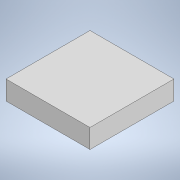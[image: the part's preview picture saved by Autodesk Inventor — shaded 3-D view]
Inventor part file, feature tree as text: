
AUTODESK INVENTOR PART (.ipt)
format: ipt  version: 2021 (Build 250183000, 183)  size: 5,559,296 bytes
history: native  units: mm
features: other x26, surface_op x18, fillet x14, sketch x9, extrude x6, revolve x4, plane x3, pattern_circular x2, loft x1
ambient origin geometry x8: Origin, YZ Plane, XZ Plane, XY Plane, X Axis, Y Axis, Z Axis, Center Point
bodies: Solid1 (feature_tree)
feature tree (83):
  plane  "Work Plane1"
  plane  "Work Plane2"
  plane  "Work Plane3"
  surface_op  "Trim1"
  surface_op  "Trim2"
  surface_op  "Trim3"
  surface_op  "Trim4"
  fillet  "Fillet5"  Radius=138.0mm
  fillet  "Fillet6"  Radius=95.0mm
  fillet  "Fillet7"  Radius=33.0mm
  fillet  "Fillet8"  Radius=110.0mm
  fillet  "Fillet9"  Radius=200.0mm
  fillet  "Fillet10"  Radius=463.0mm
  pattern_circular  "Circular Pattern1"  Count=3  [1 undecoded]
  surface_op  "Stitch Surface1"
  pattern_circular  "Circular Pattern2"  Count=20  [1 undecoded]
  surface_op  "Trim5"
  surface_op  "Trim6"
  surface_op  "Trim7"
  surface_op  "Trim8"
  surface_op  "Trim9"
  extrude  "Extrusion1"  Depth=16.0mm
  surface_op  "Sculpt1"
  sketch  "Sketch1"  dims[d6=84.0mm]
  other  "Srf1"
  sketch  "Sketch2"  dims[d7=12.566371mm d8=30.0mm]
  other  "Srf2"
  sketch  "Sketch3"  dims[d9=35.0mm d10=200.0mm]
  other  "Srf3"
  sketch  "Sketch7"  dims[d11=12.566371mm d12=16.0mm]
  sketch  "Sketch9"  dims[d13=50.0mm d14=130.0mm]
  sketch  "Sketch10"  dims[d15=245.0mm d16=369.0mm]
  other  "Srf4"
  other  "Srf5"
  other  "Srf6"
  sketch  "Sketch11"  dims[d17=63.0mm d18=12.566371mm]
  other  "Srf7"
  other  "Srf8"
  other  "Srf9"
  other  "Srf11"
  other  "Srf12"
  other  "Srf13"
  other  "Srf10"
  other  "Srf14"
  sketch  "Sketch12"  dims[d42=152.0mm d43=80.0mm d44=80.0mm]
  other  "Srf15"
  other  "Srf16"
  other  "Srf17"
  other  "Srf18"
  other  "Srf19"
  sketch  "Sketch13"  dims[d45=100.0mm d46=6.283185mm d47=6.283185mm d48=45.0mm d49=360.0mm d51=25.0mm d52=50.0mm d53=0.0mm d54=90.0deg d55=0.0mm d56=90.0deg d57=0.0mm d58=90.0deg d59=120.0mm d61=-25.0mm d62=-120.0mm d63=15.0mm d64=15.0mm d65=20.0mm d66=75.0mm d67=30.0mm d68=70.0mm d69=30.0mm d70=80.0mm d71=12.566371mm d72=5.0mm d73=5.0mm d74=5.0mm d75=5.0mm d76=5.0mm d77=5.0mm d78=5.0mm d79=5.0mm d80=50.0mm d81=360.0deg d83=300.0mm d84=80.0mm d85=10.0mm d86=0.0mm d87=50.0mm d88=360.0deg d98=1100.0mm d99=550.0mm d100=250.0mm d101=68.0mm d102=1100.0mm d103=0.0mm d116=5.0mm d117=0.0mm d118=5.0mm d119=0.0mm d120=5.0mm d121=0.0mm d122=5.0mm d123=0.0mm d124=5.0mm d125=0.0mm d126=5.0mm d127=0.0mm]
  other  "Srf28"
  other  "Srf29"
  other  "Srf30"
  other  "Srf31"
  other  "Srf32"
  other  "Srf33"
  surface_op  "Stitch Surface3"
  other  "Srf34"
  revolve  "RevolutionSrf1"  [1 undecoded]
  revolve  "RevolutionSrf2"  [1 undecoded]
  revolve  "RevolutionSrf3"  [1 undecoded]
  loft  "LoftSrf1"
  fillet  "Fillet4"  Radius=80.0mm
  extrude  "ExtrusionSrf1"  Depth=6.283185mm
  fillet  "Fillet1"  Radius=6.283185mm
  fillet  "Fillet2"  Radius=45.0mm
  revolve  "RevolutionSrf4"  [1 undecoded]
  fillet  "Fillet3"  Radius=25.0mm
  fillet  "Fillet11"  Radius=50.0mm
  fillet  "Fillet12"  [1 undecoded]
  fillet  "Fillet13"  [1 undecoded]
  fillet  "Fillet14"  [1 undecoded]
  extrude  "ExtrusionSrf2"  Depth=120.0mm
  extrude  "ExtrusionSrf3"  Depth=15.0mm
  extrude  "ExtrusionSrf4"  Depth=15.0mm
  extrude  "ExtrusionSrf5"  Depth=20.0mm
  surface_op  "Boundary Patch8"
  surface_op  "Boundary Patch9"
  surface_op  "Boundary Patch10"
  surface_op  "Boundary Patch11"
  surface_op  "Boundary Patch12"
  surface_op  "Boundary Patch13"
note: 9 required parameter values undecoded (feature->parameter linkage not recoverable at this tier; creation-order binding heuristic only, values carry confidence <= 0.55)